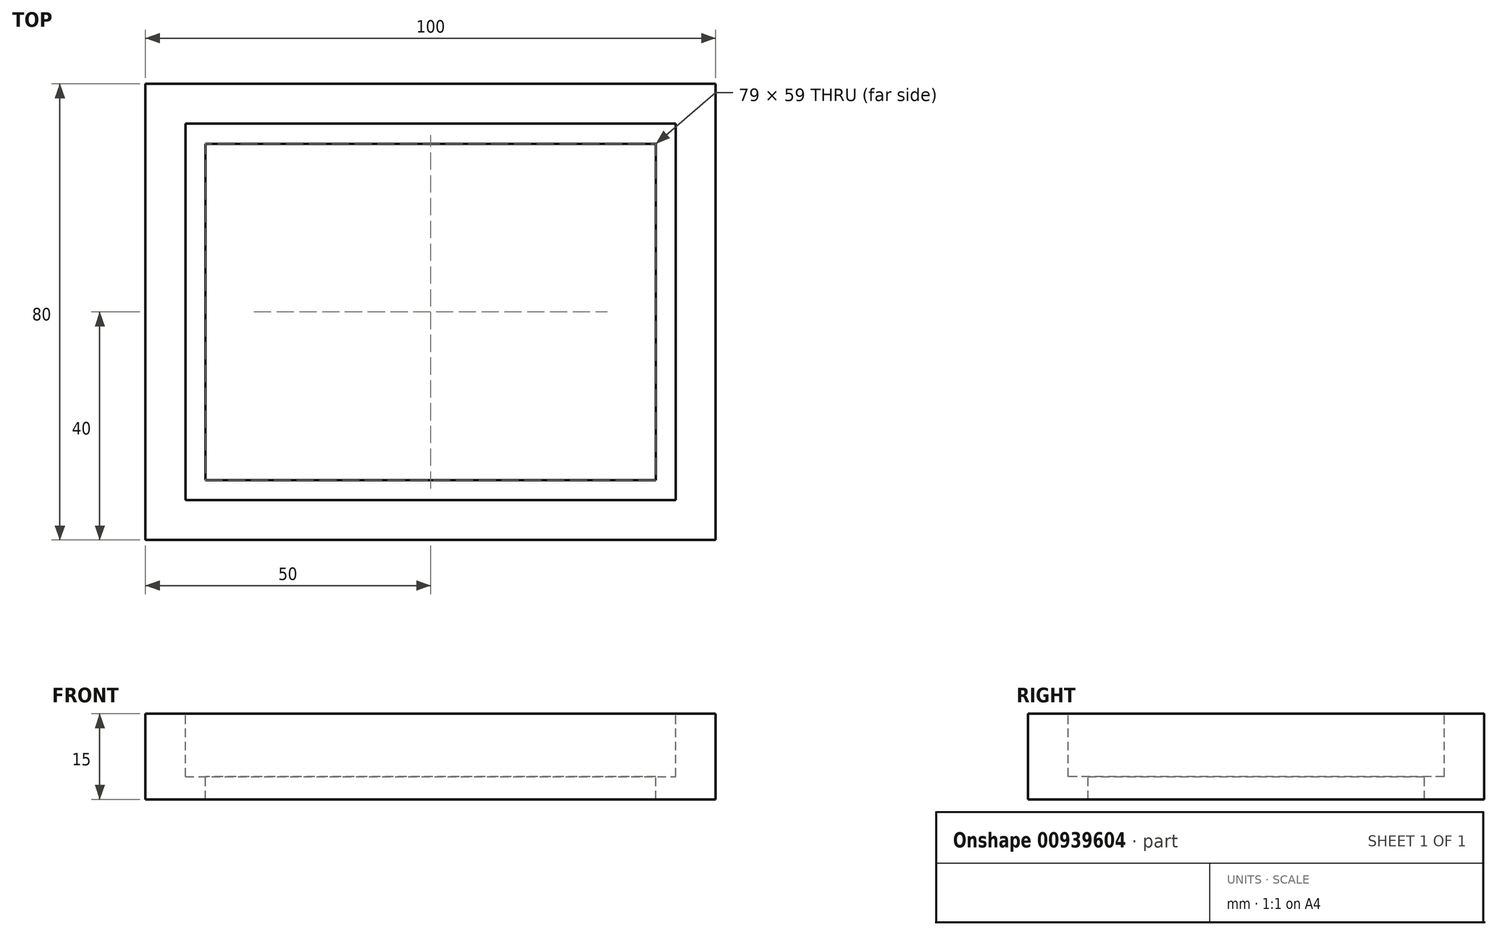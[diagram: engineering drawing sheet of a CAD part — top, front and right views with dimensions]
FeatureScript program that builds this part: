
annotation { "Feature Type Name" : "Feature", "Feature Type Description" : "" }
export const myFeature = defineFeature(function(context is Context, id is Id, definition is map)
    precondition{}
    {
        {
            var Q0;
            Q0=qCreatedBy(makeId("Top.planeOp"),FACE);
            var sketch = newSketch(context, id + "F0", { "sketchPlane" : qUnion([Q0])});
            skLineSegment(sketch, "E0.bottom", {"start": v(-50, 40) * mm, "end": v(50, 40) * mm});
            skLineSegment(sketch, "E0.top", {"start": v(-50, -40) * mm, "end": v(50, -40) * mm});
            skLineSegment(sketch, "E0.left", {"start": v(-50, 40) * mm, "end": v(-50, -40) * mm});
            skLineSegment(sketch, "E0.right", {"start": v(50, 40) * mm, "end": v(50, -40) * mm});
            skSolve(sketch);
        }
        {
            var Q0;
            Q0 = qSketchRegion(id + "F0", true);
            extrude(context, id + "F1", {"entities" : qUnion([Q0]), "depth" : 15 * mm, "offsetDistance" : 25 * mm});
        }
        {
            var Q0;
            Q0=makeQuery(id+"F1.opExtrude","CAP_FACE",FACE,{"disambiguationData":[OSD([sQuery(id+"F0.wireOp",EDGE,"E0.bottom"),sQuery(id+"F0.wireOp",EDGE,"E0.top"),sQuery(id+"F0.wireOp",EDGE,"E0.left"),sQuery(id+"F0.wireOp",EDGE,"E0.right")])],"isStart":false});
            var sketch = newSketch(context, id + "F2", { "sketchPlane" : qUnion([Q0])});
            skLineSegment(sketch, "E1.bottom", {"start": v(-43, 33) * mm, "end": v(43, 33) * mm});
            skLineSegment(sketch, "E1.top", {"start": v(-43, -33) * mm, "end": v(43, -33) * mm});
            skLineSegment(sketch, "E1.left", {"start": v(-43, 33) * mm, "end": v(-43, -33) * mm});
            skLineSegment(sketch, "E1.right", {"start": v(43, 33) * mm, "end": v(43, -33) * mm});
            skPoint(sketch, "E2", {"position": v(0, 33) * mm});
            skPoint(sketch, "E3", {"position": v(43, 0) * mm});
            skSolve(sketch);
        }
        {
            var Q0;
            Q0=makeQuery(id+"F2.imprint","IMPRINT",FACE,{"disambiguationData":[TD([[makeQuery(id+"F2.imprint","IMPRINT",EDGE,{"derivedFrom":sQuery(id+"F2.wireOp",EDGE,"E1.bottom")}),-1.0]])]});
            extrude(context, id + "F3", {"entities" : qUnion([Q0]), "operationType" : NewBodyOperationType.REMOVE, "oppositeDirection" : true, "depth" : 11 * mm, "offsetDistance" : 25 * mm});
        }
        {
            var Q0;
            Q0=makeQuery(id+"F3.boolean.opBoolean","COPY",FACE,{"derivedFrom":makeQuery(id+"F3.opExtrude","CAP_FACE",FACE,{"disambiguationData":[OSD([sQuery(id+"F2.wireOp",EDGE,"E1.bottom"),sQuery(id+"F2.wireOp",EDGE,"E1.top"),sQuery(id+"F2.wireOp",EDGE,"E1.left"),sQuery(id+"F2.wireOp",EDGE,"E1.right")])],"isStart":false})});
            var sketch = newSketch(context, id + "F4", { "sketchPlane" : qUnion([Q0])});
            skLineSegment(sketch, "E4.bottom", {"start": v(39.5, -29.5) * mm, "end": v(-39.5, -29.5) * mm});
            skLineSegment(sketch, "E4.top", {"start": v(39.5, 29.5) * mm, "end": v(-39.5, 29.5) * mm});
            skLineSegment(sketch, "E4.left", {"start": v(39.5, -29.5) * mm, "end": v(39.5, 29.5) * mm});
            skLineSegment(sketch, "E4.right", {"start": v(-39.5, -29.5) * mm, "end": v(-39.5, 29.5) * mm});
            skPoint(sketch, "E4.middle", {"position": v(0, 0) * mm});
            skSolve(sketch);
        }
        {
            var Q0;
            Q0=makeQuery(id+"F4.imprint","IMPRINT",FACE,{"disambiguationData":[TD([[makeQuery(id+"F4.imprint","IMPRINT",EDGE,{"derivedFrom":sQuery(id+"F4.wireOp",EDGE,"E4.bottom")}),-1.0]])]});
            extrude(context, id + "F5", {"entities" : qUnion([Q0]), "operationType" : NewBodyOperationType.REMOVE, "endBound" : BoundingType.THROUGH_ALL, "oppositeDirection" : true, "depth" : 25 * mm, "offsetDistance" : 25 * mm});
        }
    });
